# Revit family: 4401I_Analog Smoke Detector
name_source: partatom
category: Fire Alarm Devices
units: mm (PartAtom-declared; Revit-internal decimal feet)

## family parameters
Cut with Voids When Loaded = No
Host = Face
Maintain Annotation Orientation = No
OmniClass Number = 23.85.30.21
OmniClass Title = Environmental Detection/Registration
Part Type = Normal
Room Calculation Point = No
Round Connector Dimension = Use Diameter
Shared = No

## types (1)
- 4401I_Analog Smoke Detector
    Ambient Humidity = Maximum 95 % RH
    Ambient Temperature Operating = -10 to +50 °C
    Ambient Temperature Storage = -25 to +75 °C
    Bases = Base_4412J_4412S : 4412J
    CPR = 0786-CPR-21673
    Clearance Area = Clearance Area
    Current (Active) = 1.3 mA
    Current Quiescent = 0.3 mA
    Default Elevation = 1200 mm
    Description = Analog photoelectric smoke detector with isolator 4401I with 4412F analog base
    H_Base (mm) = 14.6 mm  [stored 0.0479003 ft]
    H_Detector (mm) = 34 mm
    H_Total (mm) = 48.6 mm  [stored 0.159449 ft]
    Ingress Protection Rating = IP41
    Manufacturer = Panasonic
    Max_Wire Size = Ø 1.2 mm (1.13 mm²)
    Min_Wire Size = Ø 0.6 mm (0.28 mm²)
    Model = 4401i
    Omniclass Code = 23.85.30.21.11.11.11
    Omniclass Description = Smoke Detectors
    Product Material = Polycarbonate_Panasonic_White
    Short Circuit Isolator = Yes (Built-in)
    Tested and Approved = EN54-7, EN54-17
    Type Comments = The photoelectric smoke detector with isolator 4401I has low profile housing. Artificial Intelligence uses smoke sensing for the fire judgement, as well as variable sensitivity and time  delay based on the smoke changes just before the alarm level is reached. 
/ 44xx can be plugged in the base. 
The base is intended for indoor use and in dry premises.
    URL = https://www.panasonic-fire-security.com
    Uniclass 2015 Code = Pr_75_80_30_27
    Uniclass 2015 Description = Fire and smoke detector bases
    Uniformat 2010  Code = D7050
    Uniformat 2010 Description = Detection and Alarm
    Vds Approval = G220004
    Version = RVT20
    Voltage Allowed = 12 – 30 VDC
    Voltage Normal = 24 VDC
    Weight = 75g
    ø (mm) = 102 mm

note: [stored X ft] marks values corroborated as IEEE doubles in the binary element streams (Revit-internal decimal feet)

## geometry (parser evidence)
native form markers: Blend x93, Sweep x14
no freeform markers — native parametric forms only
